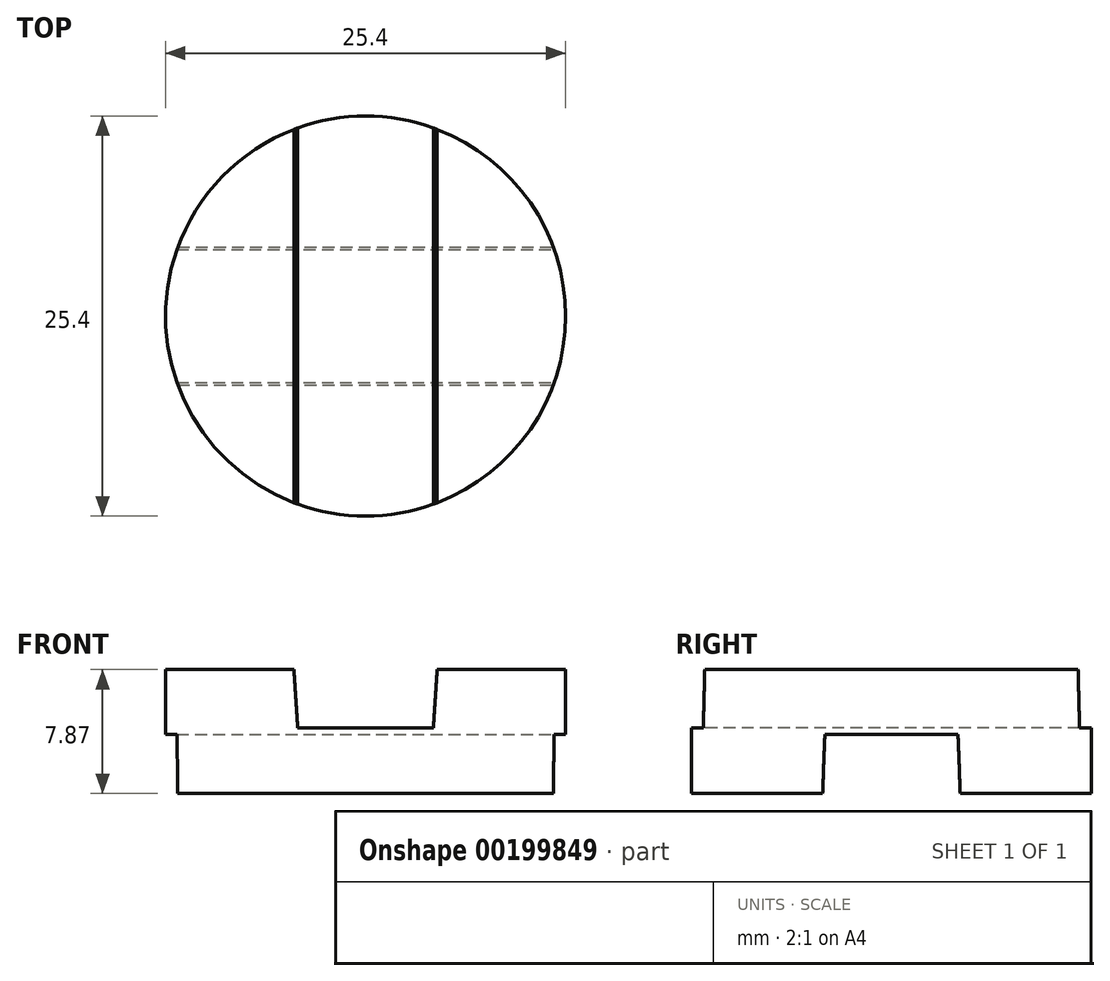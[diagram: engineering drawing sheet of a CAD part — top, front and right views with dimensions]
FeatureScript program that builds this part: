
annotation { "Feature Type Name" : "Feature", "Feature Type Description" : "" }
export const myFeature = defineFeature(function(context is Context, id is Id, definition is map)
    precondition{}
    {
        {
            var Q0;
            Q0=qCreatedBy(makeId("Top.planeOp"),FACE);
            var sketch = newSketch(context, id + "F0", { "sketchPlane" : qUnion([Q0])});
            skCircle(sketch, "E0", {"center": v(0, 0) * mm, "radius": 12.7 * mm});
            skSolve(sketch);
        }
        {
            var Q0;
            Q0 = qSketchRegion(id + "F0", true);
            extrude(context, id + "F1", {"entities" : qUnion([Q0]), "depth" : 7.87 * mm});
        }
        {
            var Q0;
            Q0=qCreatedBy(makeId("Front.planeOp"),FACE);
            var sketch = newSketch(context, id + "F2", { "sketchPlane" : qUnion([Q0])});
            skLineSegment(sketch, "E1", {"start": v(-4.55, 7.87) * mm, "end": v(4.55, 7.87) * mm});
            skLineSegment(sketch, "E2", {"start": v(4.55, 7.87) * mm, "end": v(4.3, 4.17) * mm});
            skLineSegment(sketch, "E3", {"start": v(4.3, 4.17) * mm, "end": v(-4.3, 4.17) * mm});
            skLineSegment(sketch, "E4", {"start": v(-4.3, 4.17) * mm, "end": v(-4.55, 7.87) * mm});
            skLineSegment(sketch, "E5", {"start": v(0, 7.87) * mm, "end": v(0, 4.17) * mm, "construction": true});
            skSolve(sketch);
        }
        {
            var Q0;
            Q0 = qSketchRegion(id + "F2", true);
            extrude(context, id + "F3", {"entities" : qUnion([Q0]), "operationType" : NewBodyOperationType.REMOVE, "oppositeDirection" : true, "depth" : 25.4 * mm, "hasSecondDirection" : true, "secondDirectionOppositeDirection" : false, "secondDirectionDepth" : 25.4 * mm});
        }
        {
            var Q0;
            Q0=qCreatedBy(makeId("Right.planeOp"),FACE);
            var sketch = newSketch(context, id + "F4", { "sketchPlane" : qUnion([Q0])});
            skLineSegment(sketch, "E6", {"start": v(4.23, 3.73) * mm, "end": v(-4.23, 3.73) * mm});
            skLineSegment(sketch, "E7", {"start": v(-4.23, 3.73) * mm, "end": v(-4.37, 0) * mm});
            skLineSegment(sketch, "E8", {"start": v(-4.37, 0) * mm, "end": v(4.37, 0) * mm});
            skLineSegment(sketch, "E9", {"start": v(4.37, 0) * mm, "end": v(4.23, 3.73) * mm});
            skLineSegment(sketch, "E10", {"start": v(0, 3.73) * mm, "end": v(0, 0) * mm, "construction": true});
            skSolve(sketch);
        }
        {
            var Q0;
            Q0 = qSketchRegion(id + "F4", true);
            extrude(context, id + "F5", {"entities" : qUnion([Q0]), "operationType" : NewBodyOperationType.REMOVE, "oppositeDirection" : true, "depth" : 25.4 * mm, "hasSecondDirection" : true, "secondDirectionOppositeDirection" : false, "secondDirectionDepth" : 25.4 * mm});
        }
    });
